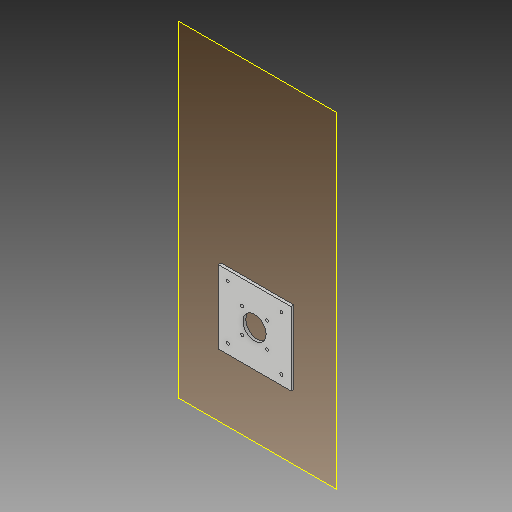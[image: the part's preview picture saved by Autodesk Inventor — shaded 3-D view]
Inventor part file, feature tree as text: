
AUTODESK INVENTOR PART (.ipt)
format: ipt  version: 2018.3 (Build 223284000, 284)  size: 95,744 bytes
history: native  units: mm
features: other x5, extrude x1, sketch x1
ambient origin geometry x8: Origin, YZ Plane, XZ Plane, XY Plane, X Axis, Y Axis, Z Axis, Center Point
bodies: Body1 (feature_tree)
feature tree (7):
  other  "Твердое тело1"
  other  "РабПлоскость1"
  extrude  "Выдавливание1"  Depth=24.0mm
  sketch  "Эскиз1"
  other  "<userpath>\GoogleDrive\My_project\Механика\Кофемашина\Inventor\Сборка.iam"
  other  "Сборка.iam"
  other  "Основание:1"
